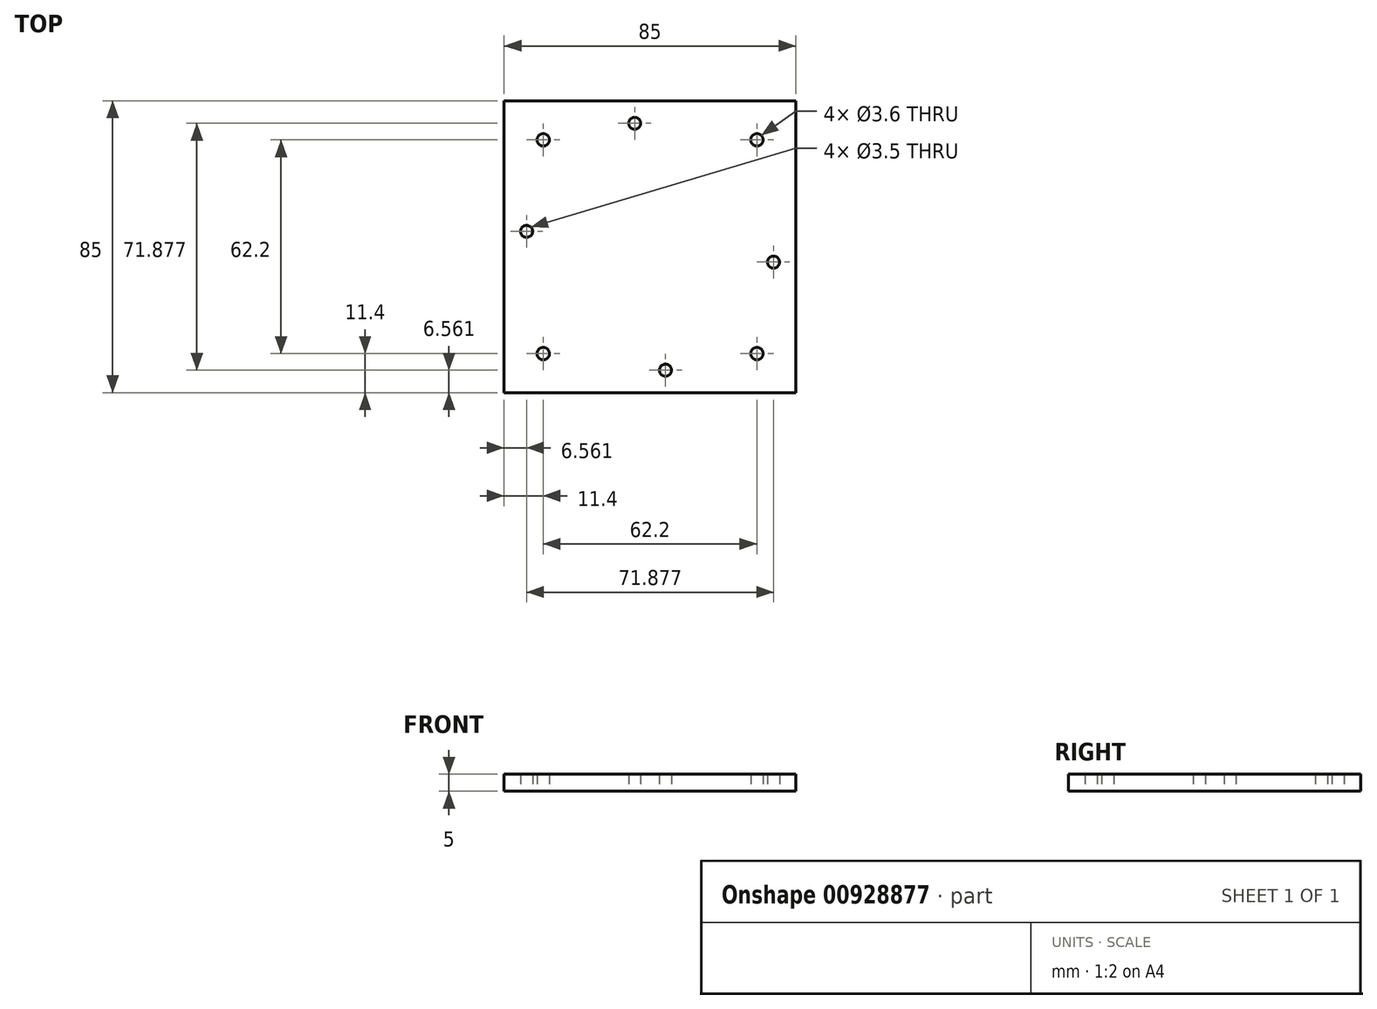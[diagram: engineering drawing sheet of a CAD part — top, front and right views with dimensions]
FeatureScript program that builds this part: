
annotation { "Feature Type Name" : "Feature", "Feature Type Description" : "" }
export const myFeature = defineFeature(function(context is Context, id is Id, definition is map)
    precondition{}
    {
        {
            var Q0;
            Q0=qCreatedBy(makeId("Top.planeOp"),FACE);
            var sketch = newSketch(context, id + "F0", { "sketchPlane" : qUnion([Q0])});
            skLineSegment(sketch, "E0.bottom", {"start": v(42.5, -42.5) * mm, "end": v(-42.5, -42.5) * mm});
            skLineSegment(sketch, "E0.top", {"start": v(42.5, 42.5) * mm, "end": v(-42.5, 42.5) * mm});
            skLineSegment(sketch, "E0.left", {"start": v(42.5, -42.5) * mm, "end": v(42.5, 42.5) * mm});
            skLineSegment(sketch, "E0.right", {"start": v(-42.5, -42.5) * mm, "end": v(-42.5, 42.5) * mm});
            skPoint(sketch, "E0.middle", {"position": v(0, 0) * mm});
            skLineSegment(sketch, "E1.bottom", {"start": v(31.1, -31.1) * mm, "end": v(-31.1, -31.1) * mm, "construction": true});
            skLineSegment(sketch, "E1.top", {"start": v(31.1, 31.1) * mm, "end": v(-31.1, 31.1) * mm, "construction": true});
            skLineSegment(sketch, "E1.left", {"start": v(31.1, -31.1) * mm, "end": v(31.1, 31.1) * mm, "construction": true});
            skLineSegment(sketch, "E1.right", {"start": v(-31.1, -31.1) * mm, "end": v(-31.1, 31.1) * mm, "construction": true});
            skCircle(sketch, "E2", {"center": v(-31.1, 31.1) * mm, "radius": 1.8 * mm});
            skCircle(sketch, "E3.MirrorC", {"center": v(31.1, 31.1) * mm, "radius": 1.8 * mm});
            skCircle(sketch, "E4.MirrorC", {"center": v(-31.1, -31.1) * mm, "radius": 1.8 * mm});
            skCircle(sketch, "E5.MirrorC", {"center": v(31.1, -31.1) * mm, "radius": 1.8 * mm});
            skSolve(sketch);
        }
        {
            var Q0;
            Q0=makeQuery(id+"F0.imprint","IMPRINT",FACE,{"disambiguationData":[TD([[makeQuery(id+"F0.imprint","IMPRINT",EDGE,{"derivedFrom":sQuery(id+"F0.wireOp",EDGE,"E0.bottom")}),-1.0]])]});
            var sketch = newSketch(context, id + "F1", { "sketchPlane" : qUnion([Q0])});
            skPoint(sketch, "E6.middle", {"position": v(0, 0) * mm});
            skLineSegment(sketch, "E7", {"start": v(-4.47, 35.94) * mm, "end": v(-35.94, 4.47) * mm, "construction": true});
            skLineSegment(sketch, "E8", {"start": v(-35.94, 4.47) * mm, "end": v(4.47, -35.94) * mm, "construction": true});
            skLineSegment(sketch, "E9", {"start": v(-4.47, 35.94) * mm, "end": v(35.94, -4.47) * mm, "construction": true});
            skLineSegment(sketch, "E10", {"start": v(35.94, -4.47) * mm, "end": v(4.47, -35.94) * mm, "construction": true});
            skCircle(sketch, "E11", {"center": v(-4.47, 35.94) * mm, "radius": 1.75 * mm});
            skCircle(sketch, "E12", {"center": v(35.94, -4.47) * mm, "radius": 1.75 * mm});
            skCircle(sketch, "E13", {"center": v(4.47, -35.94) * mm, "radius": 1.75 * mm});
            skCircle(sketch, "E14", {"center": v(-35.94, 4.47) * mm, "radius": 1.75 * mm});
            skLineSegment(sketch, "E15.bottom", {"start": v(42.5, -42.5) * mm, "end": v(-42.5, -42.5) * mm, "construction": true});
            skLineSegment(sketch, "E15.top", {"start": v(42.5, 42.5) * mm, "end": v(-42.5, 42.5) * mm, "construction": true});
            skLineSegment(sketch, "E15.left", {"start": v(42.5, -42.5) * mm, "end": v(42.5, 42.5) * mm, "construction": true});
            skLineSegment(sketch, "E15.right", {"start": v(-42.5, -42.5) * mm, "end": v(-42.5, 42.5) * mm, "construction": true});
            skSolve(sketch);
        }
        {
            var Q0;
            Q0=qSketchRegion(id+"F0",true);
            var Q1;
            Q1=qCreatedBy(makeId("Right.planeOp"),FACE);
            extrude(context, id + "F2", {"entities" : qUnion([Q0]), "depth" : 5 * mm, "endBoundEntityFace" : qUnion([Q1]), "offsetDistance" : 25 * mm});
        }
        {
            var Q0;
            Q0=qSketchRegion(id+"F1",true);
            extrude(context, id + "F3", {"entities" : qUnion([Q0]), "operationType" : NewBodyOperationType.REMOVE, "depth" : 10 * mm, "offsetDistance" : 25 * mm});
        }
    });
